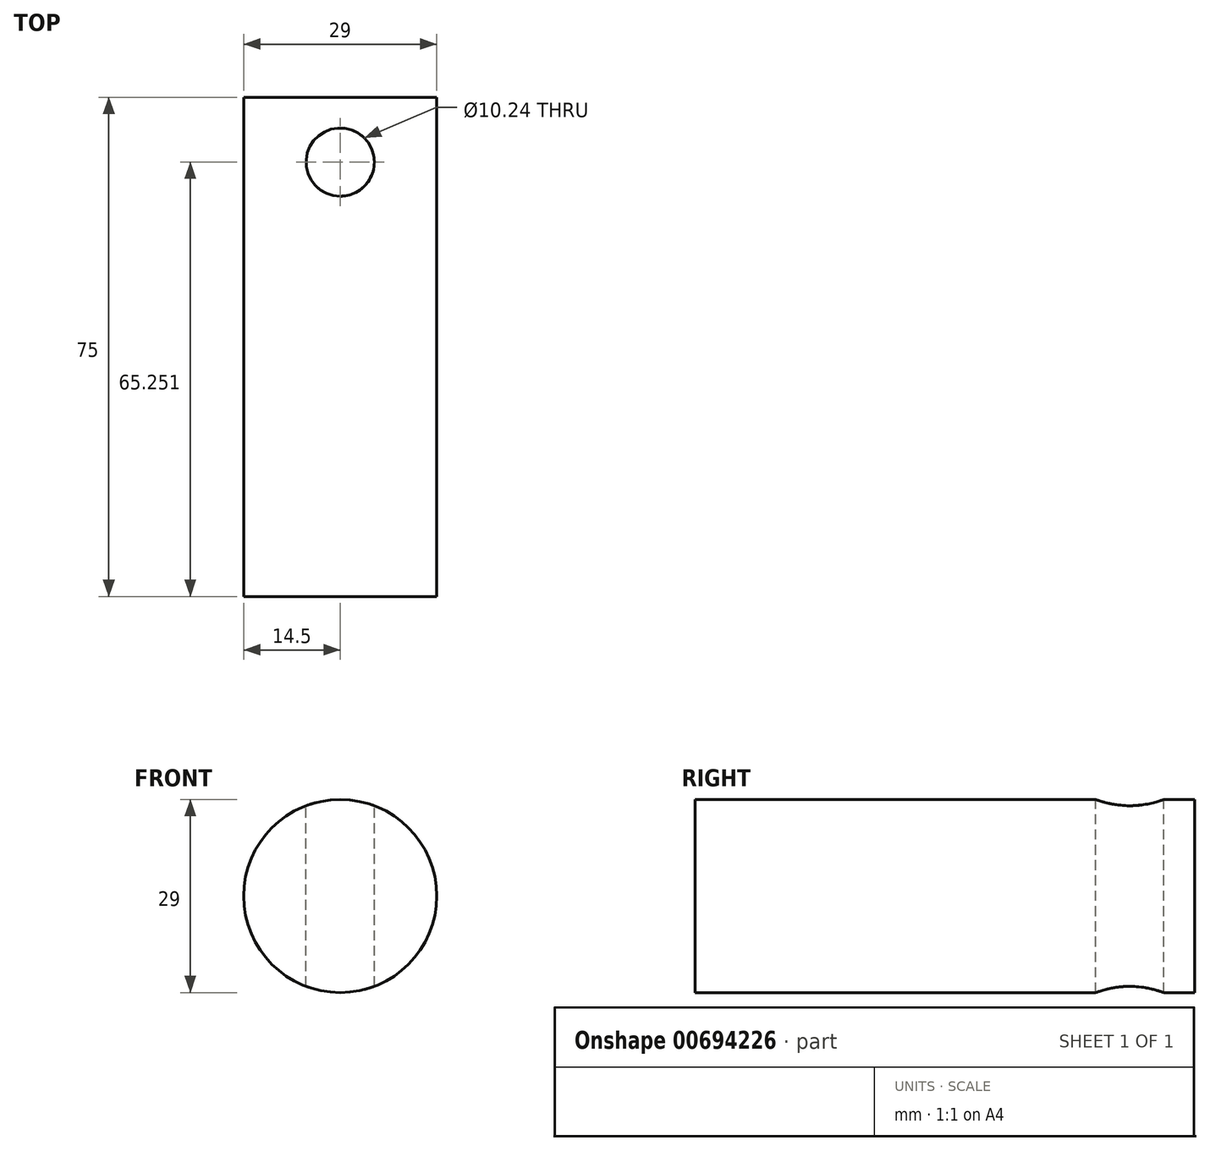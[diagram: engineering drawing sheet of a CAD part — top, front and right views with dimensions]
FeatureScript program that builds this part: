
annotation { "Feature Type Name" : "Feature", "Feature Type Description" : "" }
export const myFeature = defineFeature(function(context is Context, id is Id, definition is map)
    precondition{}
    {
        {
            var Q0;
            Q0=qCreatedBy(makeId("Front.planeOp"),FACE);
            var sketch = newSketch(context, id + "F0", { "sketchPlane" : qUnion([Q0])});
            skCircle(sketch, "E0", {"center": v(0, 0) * mm, "radius": 14.5 * mm});
            skSolve(sketch);
        }
        {
            var Q0;
            Q0=makeQuery(id+"F0.imprint","IMPRINT",FACE,{"disambiguationData":[TD([[makeQuery(id+"F0.imprint","IMPRINT",EDGE,{"derivedFrom":sQuery(id+"F0.wireOp",EDGE,"E0")}),1.0]])]});
            extrude(context, id + "F1", {"entities" : qUnion([Q0]), "endBound" : BoundingType.SYMMETRIC, "depth" : 75 * mm, "offsetDistance" : 25 * mm});
        }
        {
            var Q0;
            Q0=qCreatedBy(makeId("Top.planeOp"),FACE);
            var sketch = newSketch(context, id + "F2", { "sketchPlane" : qUnion([Q0])});
            skCircle(sketch, "E1", {"center": v(0, 27.75) * mm, "radius": 5.12 * mm});
            skSolve(sketch);
        }
        {
            var Q0;
            Q0 = qSketchRegion(id + "F2", true);
            extrude(context, id + "F3", {"entities" : qUnion([Q0]), "operationType" : NewBodyOperationType.REMOVE, "endBound" : BoundingType.SYMMETRIC, "oppositeDirection" : true, "depth" : 30 * mm, "offsetDistance" : 25 * mm});
        }
    });
